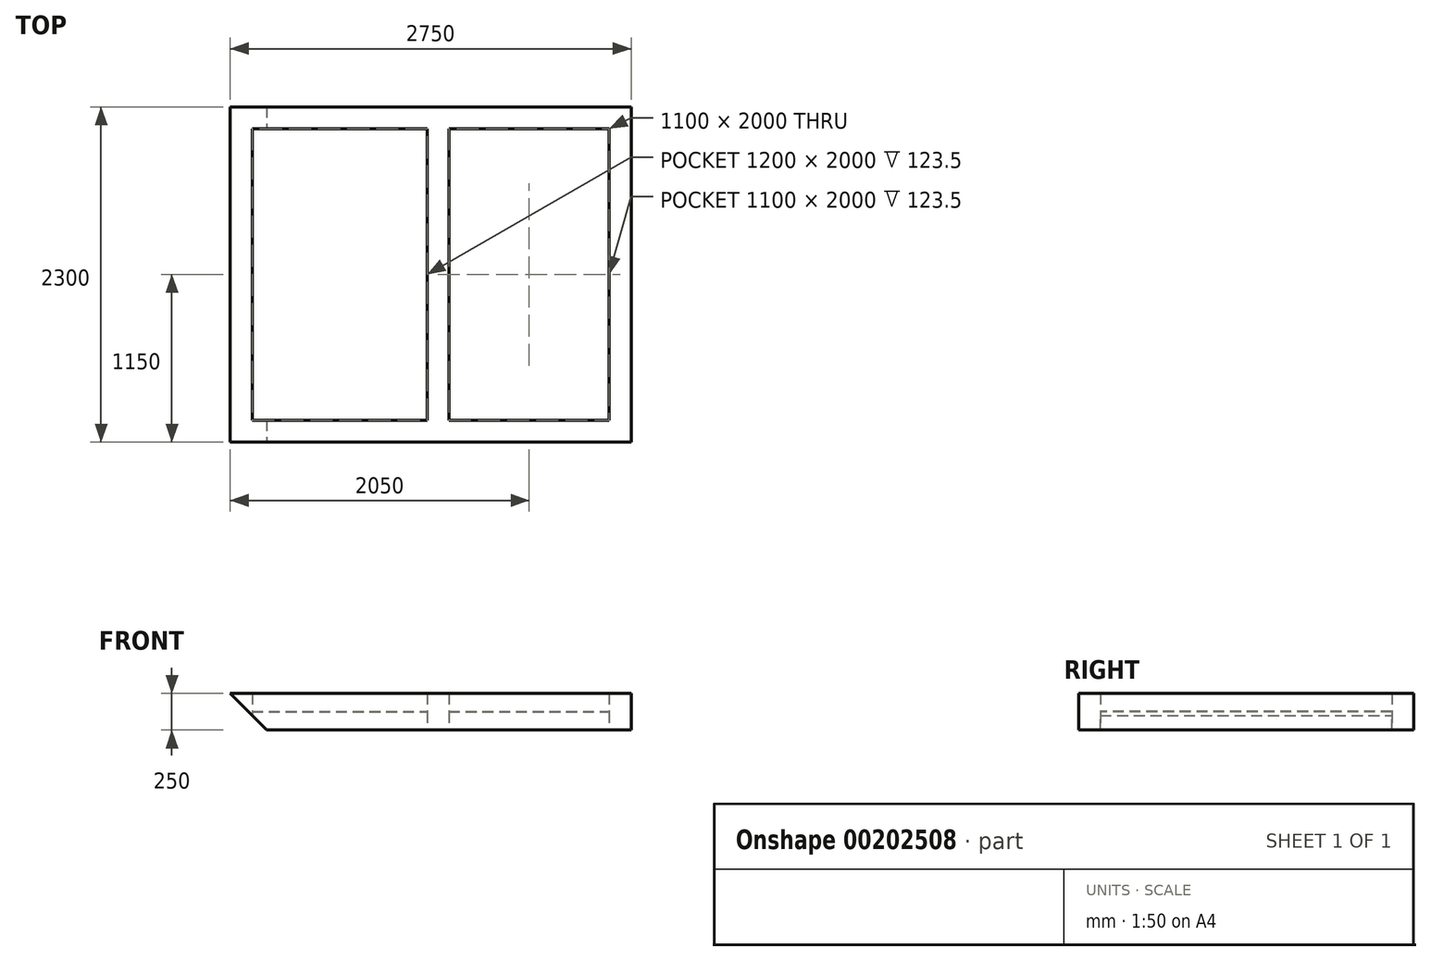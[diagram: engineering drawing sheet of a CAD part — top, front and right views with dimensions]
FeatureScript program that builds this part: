
annotation { "Feature Type Name" : "Feature", "Feature Type Description" : "" }
export const myFeature = defineFeature(function(context is Context, id is Id, definition is map)
    precondition{}
    {
        {
            var Q0;
            Q0=qCreatedBy(makeId("Top.planeOp"),FACE);
            var sketch = newSketch(context, id + "F0", { "sketchPlane" : qUnion([Q0])});
            skLineSegment(sketch, "E0.bottom", {"start": v(1375, 1150) * mm, "end": v(-1375, 1150) * mm});
            skLineSegment(sketch, "E0.top", {"start": v(1375, -1150) * mm, "end": v(-1375, -1150) * mm});
            skLineSegment(sketch, "E0.left", {"start": v(1375, 1150) * mm, "end": v(1375, -1150) * mm});
            skLineSegment(sketch, "E0.right", {"start": v(-1375, 1150) * mm, "end": v(-1375, -1150) * mm});
            skPoint(sketch, "E0.middle", {"position": v(0, 0) * mm});
            skLineSegment(sketch, "E1.bottom", {"start": v(-1225, 1000) * mm, "end": v(-25, 1000) * mm});
            skLineSegment(sketch, "E1.top", {"start": v(-1225, -1000) * mm, "end": v(-25, -1000) * mm});
            skLineSegment(sketch, "E1.left", {"start": v(-1225, 1000) * mm, "end": v(-1225, -1000) * mm});
            skLineSegment(sketch, "E1.right", {"start": v(-25, 1000) * mm, "end": v(-25, -1000) * mm});
            skLineSegment(sketch, "E2.bottom", {"start": v(125, 1000) * mm, "end": v(1225, 1000) * mm});
            skLineSegment(sketch, "E2.top", {"start": v(125, -1000) * mm, "end": v(1225, -1000) * mm});
            skLineSegment(sketch, "E2.left", {"start": v(125, 1000) * mm, "end": v(125, -1000) * mm});
            skLineSegment(sketch, "E2.right", {"start": v(1225, 1000) * mm, "end": v(1225, -1000) * mm});
            skSolve(sketch);
        }
        {
            var Q0;
            Q0=makeQuery(id+"F0.imprint","IMPRINT",FACE,{"disambiguationData":[TD([[makeQuery(id+"F0.imprint","IMPRINT",EDGE,{"derivedFrom":sQuery(id+"F0.wireOp",EDGE,"E0.bottom")}),1.0]])]});
            extrude(context, id + "F1", {"entities" : qUnion([Q0]), "endBound" : BoundingType.SYMMETRIC, "depth" : 250 * mm});
        }
        {
            var Q0;
            Q0=qCreatedBy(makeId("Top.planeOp"),FACE);
            var sketch = newSketch(context, id + "F2", { "sketchPlane" : qUnion([Q0])});
            skLineSegment(sketch, "E3.bottom", {"start": v(-1326.15, 1104.49) * mm, "end": v(-24.84, 1104.49) * mm});
            skLineSegment(sketch, "E3.top", {"start": v(-1326.15, -1098.43) * mm, "end": v(-24.84, -1098.43) * mm});
            skLineSegment(sketch, "E3.left", {"start": v(-1326.15, 1104.49) * mm, "end": v(-1326.15, -1098.43) * mm});
            skLineSegment(sketch, "E3.right", {"start": v(-24.84, 1104.49) * mm, "end": v(-24.84, -1098.43) * mm});
            skLineSegment(sketch, "E4.bottom", {"start": v(23.55, 1103.2) * mm, "end": v(1325.26, 1103.2) * mm});
            skLineSegment(sketch, "E4.top", {"start": v(23.55, -1098.43) * mm, "end": v(1325.26, -1098.43) * mm});
            skLineSegment(sketch, "E4.left", {"start": v(23.55, 1103.2) * mm, "end": v(23.55, -1098.43) * mm});
            skLineSegment(sketch, "E4.right", {"start": v(1325.26, 1103.2) * mm, "end": v(1325.26, -1098.43) * mm});
            skSolve(sketch);
        }
        {
            var Q0;
            Q0=makeQuery(id+"F2.imprint","IMPRINT",FACE,{"disambiguationData":[TD([[makeQuery(id+"F2.imprint","IMPRINT",EDGE,{"derivedFrom":sQuery(id+"F2.wireOp",EDGE,"E4.bottom")}),-1.0]])]});
            var Q1;
            Q1=makeQuery(id+"F2.imprint","IMPRINT",FACE,{"disambiguationData":[TD([[makeQuery(id+"F2.imprint","IMPRINT",EDGE,{"derivedFrom":sQuery(id+"F2.wireOp",EDGE,"E3.bottom")}),-1.0]])]});
            extrude(context, id + "F3", {"entities" : qUnion([Q0, Q1]), "operationType" : NewBodyOperationType.ADD, "endBound" : BoundingType.SYMMETRIC, "depth" : 3 * mm});
        }
        {
            var Q0;
            Q0=makeQuery(id+"F1.opExtrude","SWEPT_FACE",FACE,{"disambiguationData":[OSD([sQuery(id+"F0.wireOp",EDGE,"E0.top")])]});
            var sketch = newSketch(context, id + "F4", { "sketchPlane" : qUnion([Q0])});
            skLineSegment(sketch, "E5.top", {"start": v(-1375, -125) * mm, "end": v(-1125, -125) * mm});
            skLineSegment(sketch, "E5.left", {"start": v(-1375, 125) * mm, "end": v(-1375, -125) * mm});
            skLineSegment(sketch, "E6", {"start": v(-1375, 125) * mm, "end": v(-1125, -125) * mm});
            skSolve(sketch);
        }
        {
            var Q0;
            Q0=makeQuery(id+"F4.imprint","IMPRINT",FACE,{"disambiguationData":[TD([[makeQuery(id+"F4.imprint","IMPRINT",EDGE,{"derivedFrom":sQuery(id+"F4.wireOp",EDGE,"E5.top")}),-1.0]])]});
            var Q1;
            Q1=makeQuery(id+"F1.opExtrude","SWEPT_FACE",FACE,{"disambiguationData":[OSD([sQuery(id+"F0.wireOp",EDGE,"E0.bottom")])]});
            extrude(context, id + "F5", {"entities" : qUnion([Q0]), "operationType" : NewBodyOperationType.REMOVE, "endBound" : BoundingType.UP_TO_SURFACE, "oppositeDirection" : true, "endBoundEntityFace" : qUnion([Q1]), "depth" : 25 * mm});
        }
    });
